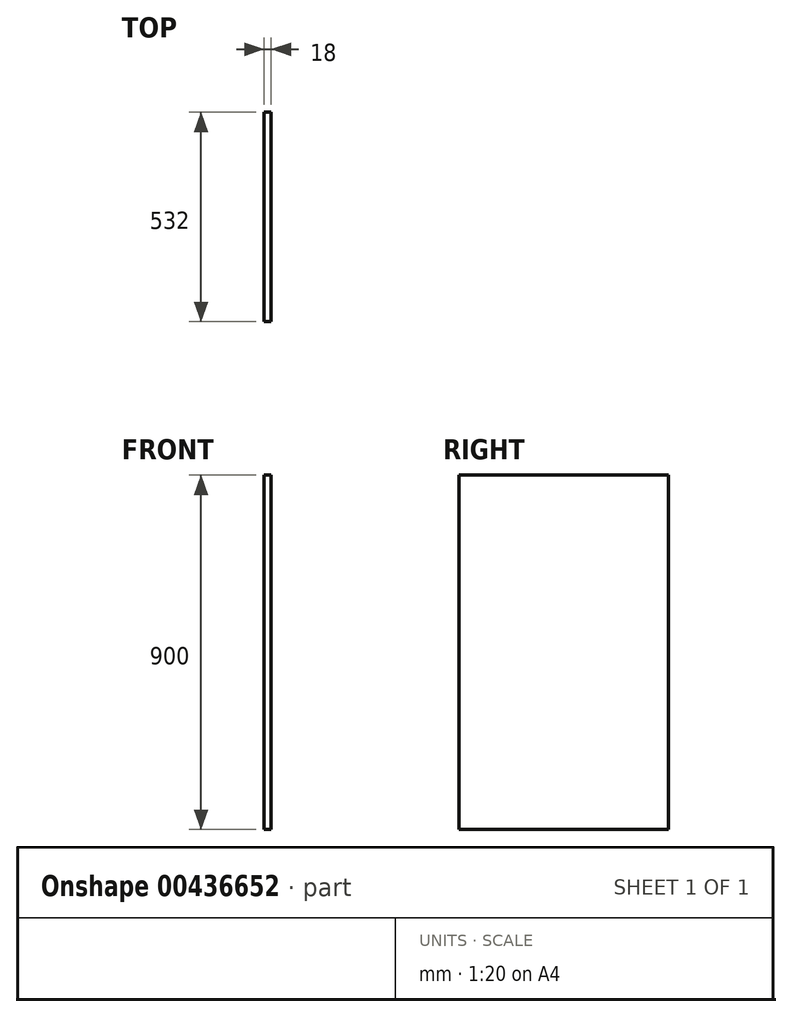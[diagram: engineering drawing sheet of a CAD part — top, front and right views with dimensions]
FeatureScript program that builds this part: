
annotation { "Feature Type Name" : "Feature", "Feature Type Description" : "" }
export const myFeature = defineFeature(function(context is Context, id is Id, definition is map)
    precondition{}
    {
        {
            var Q0;
            Q0=qCreatedBy(makeId("Right.planeOp"),FACE);
            var sketch = newSketch(context, id + "F0", { "sketchPlane" : qUnion([Q0])});
            skLineSegment(sketch, "E0.bottom", {"start": v(266, 450) * mm, "end": v(-266, 450) * mm});
            skLineSegment(sketch, "E0.top", {"start": v(266, -450) * mm, "end": v(-266, -450) * mm});
            skLineSegment(sketch, "E0.left", {"start": v(266, 450) * mm, "end": v(266, -450) * mm});
            skLineSegment(sketch, "E0.right", {"start": v(-266, 450) * mm, "end": v(-266, -450) * mm});
            skPoint(sketch, "E0.middle", {"position": v(0, 0) * mm});
            skSolve(sketch);
        }
        {
            var Q0;
            Q0=qSketchRegion(id+"F0",true);
            extrude(context, id + "F1", {"entities" : qUnion([Q0]), "depth" : 18 * mm});
        }
    });
